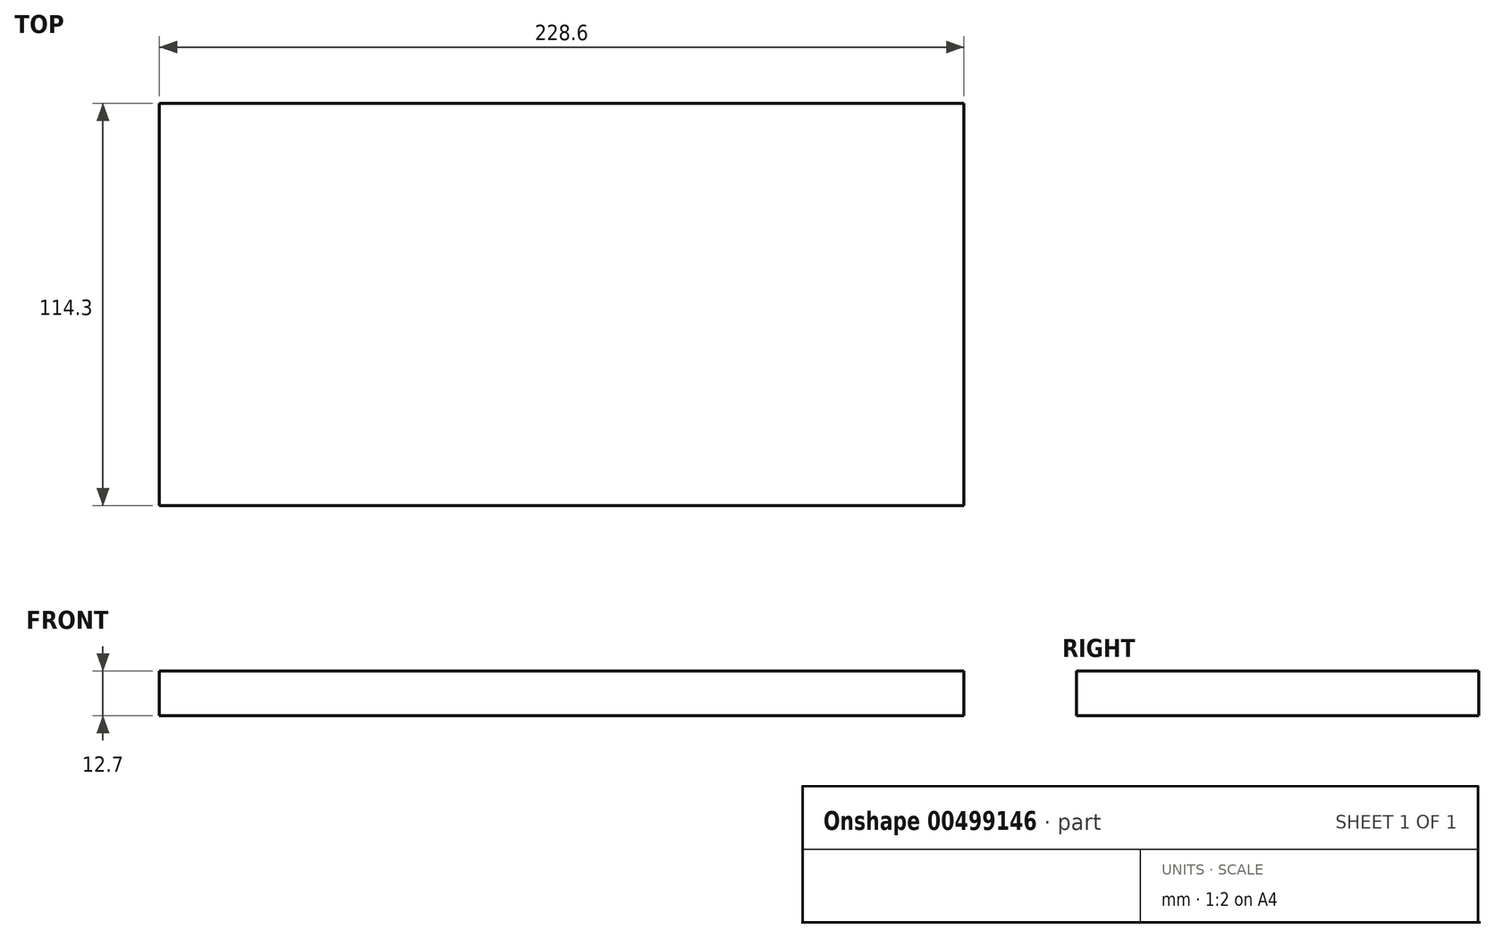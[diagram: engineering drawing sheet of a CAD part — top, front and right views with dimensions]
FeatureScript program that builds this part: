
annotation { "Feature Type Name" : "Feature", "Feature Type Description" : "" }
export const myFeature = defineFeature(function(context is Context, id is Id, definition is map)
    precondition{}
    {
        {
            var Q0;
            Q0=qCreatedBy(makeId("Top.planeOp"),FACE);
            var sketch = newSketch(context, id + "F0", { "sketchPlane" : qUnion([Q0])});
            skLineSegment(sketch, "E0.bottom", {"start": v(114.3, 57.15) * mm, "end": v(-114.3, 57.15) * mm});
            skLineSegment(sketch, "E0.top", {"start": v(114.3, -57.15) * mm, "end": v(-114.3, -57.15) * mm});
            skLineSegment(sketch, "E0.left", {"start": v(114.3, 57.15) * mm, "end": v(114.3, -57.15) * mm});
            skLineSegment(sketch, "E0.right", {"start": v(-114.3, 57.15) * mm, "end": v(-114.3, -57.15) * mm});
            skPoint(sketch, "E0.middle", {"position": v(0, 0) * mm});
            skLineSegment(sketch, "E1", {"start": v(0, 0) * mm, "end": v(65.25, 0) * mm});
            skLineSegment(sketch, "E2", {"start": v(65.25, 0) * mm, "end": v(0, 0) * mm, "construction": true});
            skLineSegment(sketch, "E3", {"start": v(-65.25, 0) * mm, "end": v(0, 0) * mm, "construction": true});
            skPoint(sketch, "E4", {"position": v(-65.25, 0) * mm});
            skPoint(sketch, "E5", {"position": v(65.25, 0) * mm});
            skPoint(sketch, "E6", {"position": v(126.87, 10.64) * mm});
            skLineSegment(sketch, "E7", {"start": v(0, 0) * mm, "end": v(114.3, 0) * mm});
            skSolve(sketch);
        }
        {
            var Q0;
            Q0=makeQuery(id+"F0.imprint","IMPRINT",FACE,{"disambiguationData":[TD([[makeQuery(id+"F0.imprint","IMPRINT",EDGE,{"derivedFrom":sQuery(id+"F0.wireOp",EDGE,"E0.bottom")}),1.0]])]});
            extrude(context, id + "F1", {"entities" : qUnion([Q0]), "depth" : 12.7 * mm});
        }
    });
